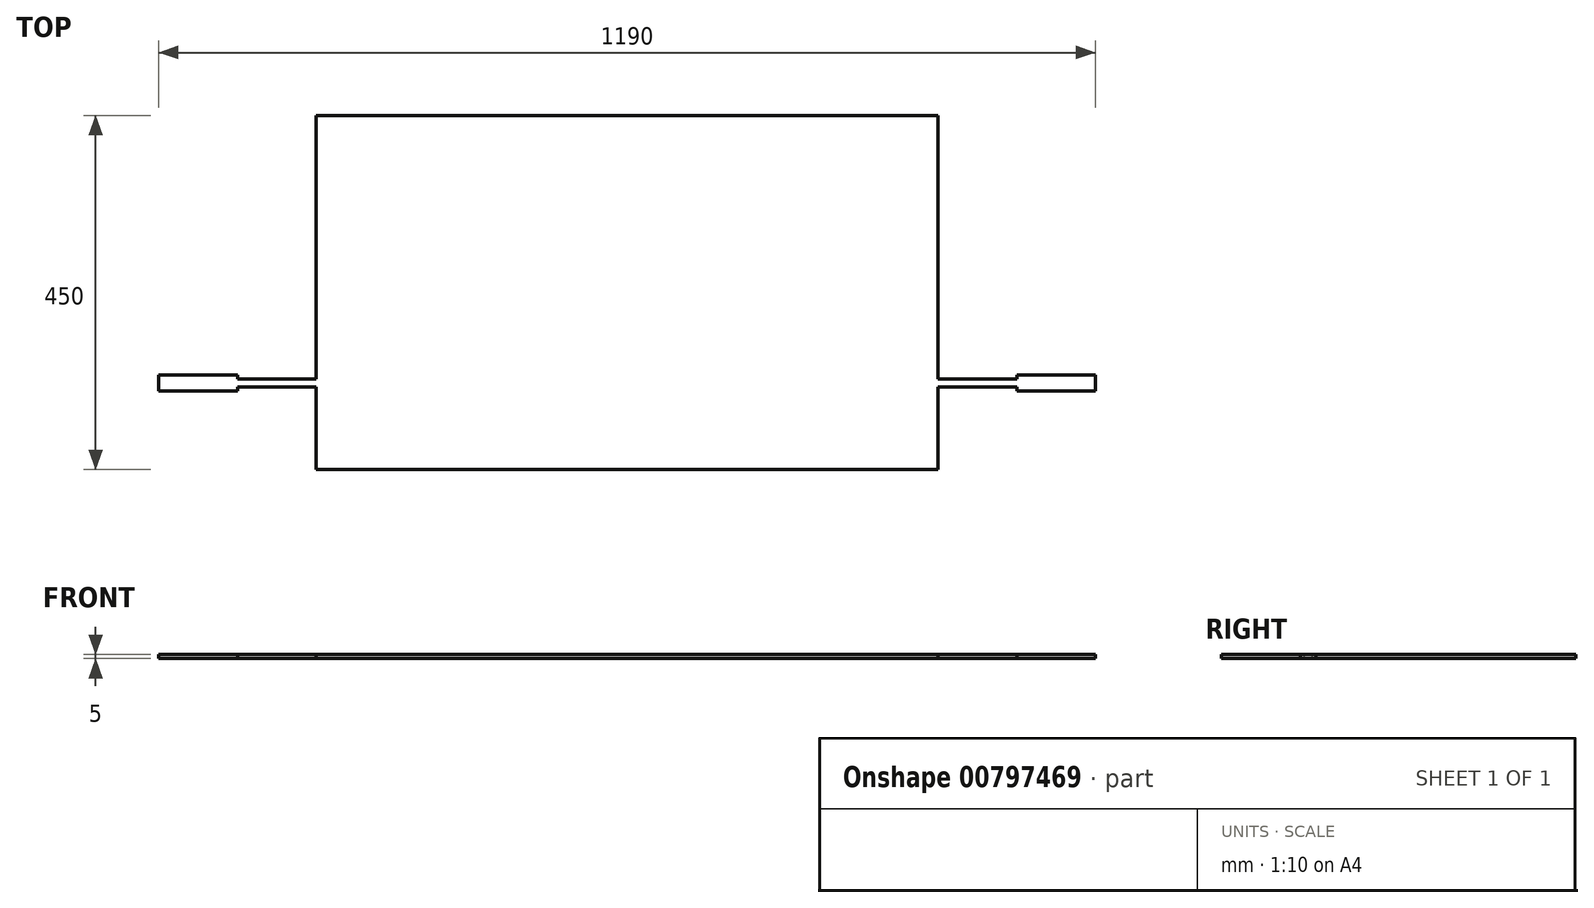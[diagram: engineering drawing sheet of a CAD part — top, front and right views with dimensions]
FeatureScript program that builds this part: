
annotation { "Feature Type Name" : "Feature", "Feature Type Description" : "" }
export const myFeature = defineFeature(function(context is Context, id is Id, definition is map)
    precondition{}
    {
        {
            var Q0;
            Q0=qCreatedBy(makeId("Top.planeOp"),FACE);
            var sketch = newSketch(context, id + "F0", { "sketchPlane" : qUnion([Q0])});
            skLineSegment(sketch, "E0", {"start": v(-485.24, 261.7) * mm, "end": v(304.76, 261.7) * mm});
            skLineSegment(sketch, "E1", {"start": v(304.76, 261.7) * mm, "end": v(304.76, -73.3) * mm});
            skLineSegment(sketch, "E2", {"start": v(304.76, -73.3) * mm, "end": v(404.76, -73.3) * mm});
            skLineSegment(sketch, "E3", {"start": v(404.76, -73.3) * mm, "end": v(404.76, -68.3) * mm});
            skLineSegment(sketch, "E4", {"start": v(404.76, -68.3) * mm, "end": v(504.76, -68.3) * mm});
            skLineSegment(sketch, "E5", {"start": v(504.76, -68.3) * mm, "end": v(504.76, -88.3) * mm});
            skLineSegment(sketch, "E6", {"start": v(504.76, -88.3) * mm, "end": v(404.76, -88.3) * mm});
            skLineSegment(sketch, "E7", {"start": v(404.76, -88.3) * mm, "end": v(404.76, -83.3) * mm});
            skLineSegment(sketch, "E8", {"start": v(404.76, -83.3) * mm, "end": v(304.76, -83.3) * mm});
            skLineSegment(sketch, "E9", {"start": v(304.76, -83.3) * mm, "end": v(304.76, -188.3) * mm});
            skLineSegment(sketch, "E10", {"start": v(304.76, -188.3) * mm, "end": v(-485.24, -188.3) * mm});
            skLineSegment(sketch, "E11", {"start": v(-485.24, -188.3) * mm, "end": v(-485.24, -83.3) * mm});
            skLineSegment(sketch, "E12", {"start": v(-485.24, -83.3) * mm, "end": v(-585.24, -83.3) * mm});
            skLineSegment(sketch, "E13", {"start": v(-585.24, -83.3) * mm, "end": v(-585.24, -88.3) * mm});
            skLineSegment(sketch, "E14", {"start": v(-585.24, -88.3) * mm, "end": v(-685.24, -88.3) * mm});
            skLineSegment(sketch, "E15", {"start": v(-685.24, -88.3) * mm, "end": v(-685.24, -68.3) * mm});
            skLineSegment(sketch, "E16", {"start": v(-685.24, -68.3) * mm, "end": v(-585.24, -68.3) * mm});
            skLineSegment(sketch, "E17", {"start": v(-585.24, -68.3) * mm, "end": v(-585.24, -73.3) * mm});
            skLineSegment(sketch, "E18", {"start": v(-585.24, -73.3) * mm, "end": v(-485.24, -73.3) * mm});
            skLineSegment(sketch, "E19", {"start": v(-485.24, -73.3) * mm, "end": v(-485.24, 261.7) * mm});
            skSolve(sketch);
        }
        {
            var Q0;
            Q0=makeQuery(id+"F0.imprint","IMPRINT",FACE,{"disambiguationData":[TD([[makeQuery(id+"F0.imprint","IMPRINT",EDGE,{"derivedFrom":sQuery(id+"F0.wireOp",EDGE,"E0")}),-1.0]])]});
            extrude(context, id + "F1", {"entities" : qUnion([Q0]), "depth" : 5 * mm, "offsetDistance" : 25 * mm});
        }
    });
